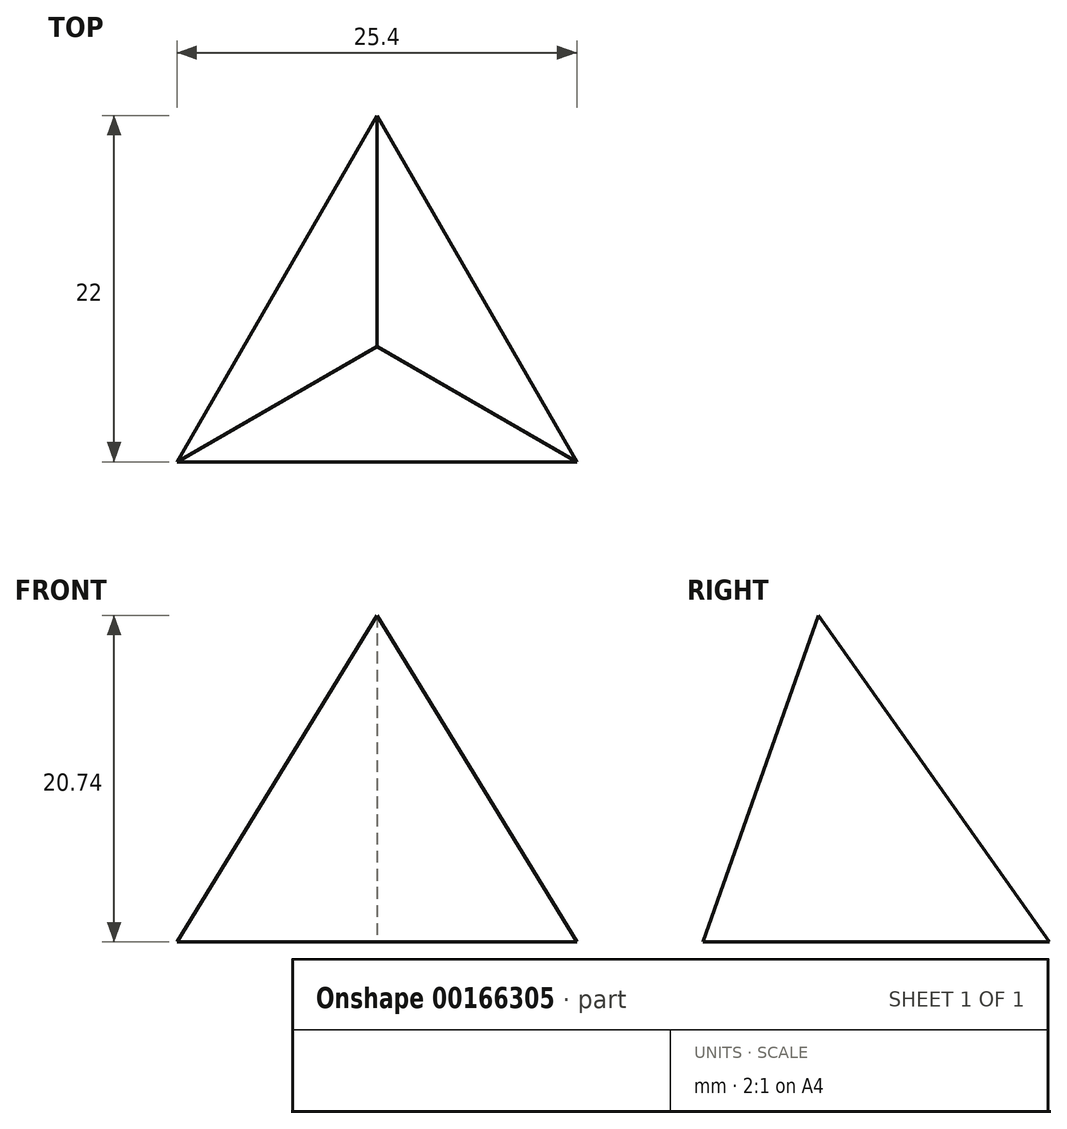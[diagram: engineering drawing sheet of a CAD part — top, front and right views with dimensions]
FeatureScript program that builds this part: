
annotation { "Feature Type Name" : "Feature", "Feature Type Description" : "" }
export const myFeature = defineFeature(function(context is Context, id is Id, definition is map)
    precondition{}
    {
        {
            var Q0;
            Q0=qCreatedBy(makeId("Top.planeOp"),FACE);
            var sketch = newSketch(context, id + "F0", { "sketchPlane" : qUnion([Q0])});
            skLineSegment(sketch, "E0", {"start": v(-12.7, 0) * mm, "end": v(0, 22) * mm});
            skLineSegment(sketch, "E1", {"start": v(0, 22) * mm, "end": v(12.7, 0) * mm});
            skLineSegment(sketch, "E2", {"start": v(12.7, 0) * mm, "end": v(-12.7, 0) * mm});
            skSolve(sketch);
        }
        {
            var Q0;
            Q0=makeQuery(id+"F0.imprint","IMPRINT",FACE,{"disambiguationData":[TD([[makeQuery(id+"F0.imprint","IMPRINT",EDGE,{"derivedFrom":sQuery(id+"F0.wireOp",EDGE,"E0")}),-1.0]])]});
            extrude(context, id + "F1", {"entities" : qUnion([Q0]), "depth" : 26.42 * mm, "hasDraft" : true, "draftAngle" : 90 * degree - atan(2 * (2 ^ 0.5)), "draftPullDirection" : true});
        }
    });
